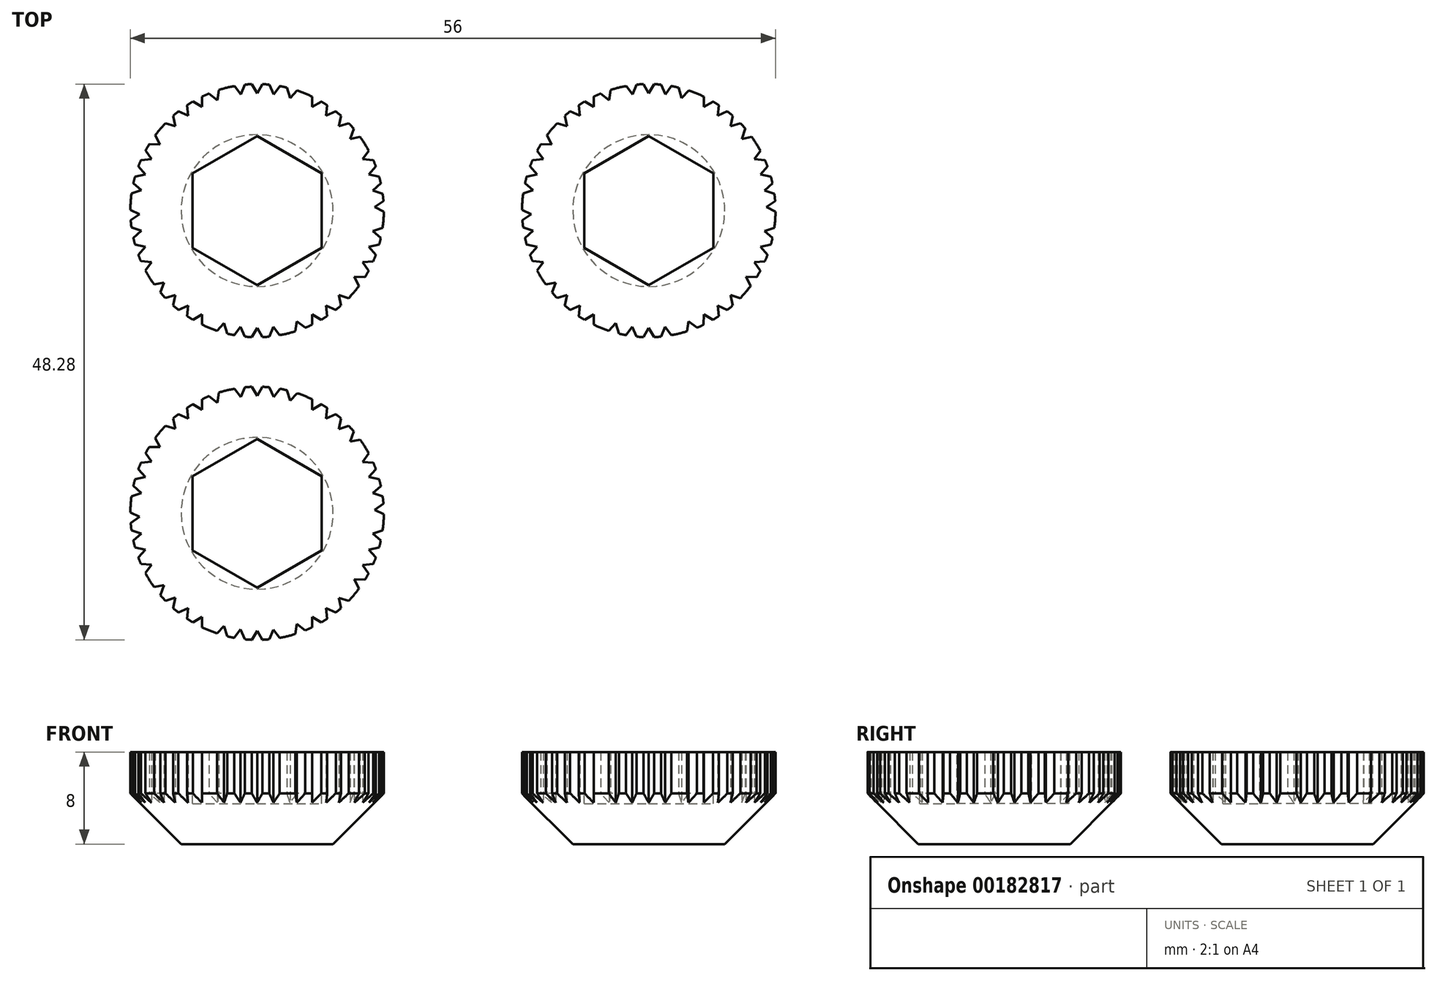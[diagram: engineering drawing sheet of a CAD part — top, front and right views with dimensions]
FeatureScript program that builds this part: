
annotation { "Feature Type Name" : "Feature", "Feature Type Description" : "" }
export const myFeature = defineFeature(function(context is Context, id is Id, definition is map)
    precondition{}
    {
        {
            var Q0;
            Q0=qCreatedBy(makeId("Top.planeOp"),FACE);
            var sketch = newSketch(context, id + "F0", { "sketchPlane" : qUnion([Q0])});
            skCircle(sketch, "E0", {"center": v(0, 0) * mm, "radius": 11 * mm});
            skCircle(sketch, "E1.cCircle", {"center": v(0, 11) * mm, "radius": 0.4 * mm, "construction": true});
            skLineSegment(sketch, "E1.0", {"start": v(-0.7, 11.4) * mm, "end": v(0.7, 11.4) * mm});
            skLineSegment(sketch, "E1.1", {"start": v(0.7, 11.4) * mm, "end": v(0, 10.2) * mm});
            skLineSegment(sketch, "E1.2", {"start": v(0, 10.2) * mm, "end": v(-0.7, 11.4) * mm});
            skPoint(sketch, "E1.0.midPoint", {"position": v(0, 11.4) * mm});
            skLineSegment(sketch, "E2.1.0", {"start": v(-6, 8.25) * mm, "end": v(-7.26, 8.82) * mm});
            skCircle(sketch, "E2.1.1", {"center": v(-6.47, 8.9) * mm, "radius": 0.4 * mm, "construction": true});
            skPoint(sketch, "E2.1.2", {"position": v(-6.7, 9.22) * mm});
            skLineSegment(sketch, "E2.1.3", {"start": v(-7.26, 8.82) * mm, "end": v(-6.14, 9.63) * mm});
            skLineSegment(sketch, "E2.1.4", {"start": v(-6.14, 9.63) * mm, "end": v(-6, 8.25) * mm});
            skLineSegment(sketch, "E2.2.0", {"start": v(-9.7, 3.15) * mm, "end": v(-11.06, 2.86) * mm});
            skCircle(sketch, "E2.2.1", {"center": v(-10.46, 3.4) * mm, "radius": 0.4 * mm, "construction": true});
            skPoint(sketch, "E2.2.2", {"position": v(-10.84, 3.52) * mm});
            skLineSegment(sketch, "E2.2.3", {"start": v(-11.06, 2.86) * mm, "end": v(-10.63, 4.18) * mm});
            skLineSegment(sketch, "E2.2.4", {"start": v(-10.63, 4.18) * mm, "end": v(-9.7, 3.15) * mm});
            skLineSegment(sketch, "E2.3.0", {"start": v(-9.7, -3.15) * mm, "end": v(-10.63, -4.18) * mm});
            skCircle(sketch, "E2.3.1", {"center": v(-10.46, -3.4) * mm, "radius": 0.4 * mm, "construction": true});
            skPoint(sketch, "E2.3.2", {"position": v(-10.84, -3.52) * mm});
            skLineSegment(sketch, "E2.3.3", {"start": v(-10.63, -4.18) * mm, "end": v(-11.06, -2.86) * mm});
            skLineSegment(sketch, "E2.3.4", {"start": v(-11.06, -2.86) * mm, "end": v(-9.7, -3.15) * mm});
            skLineSegment(sketch, "E2.4.0", {"start": v(-6, -8.25) * mm, "end": v(-6.14, -9.63) * mm});
            skCircle(sketch, "E2.4.1", {"center": v(-6.47, -8.9) * mm, "radius": 0.4 * mm, "construction": true});
            skPoint(sketch, "E2.4.2", {"position": v(-6.7, -9.22) * mm});
            skLineSegment(sketch, "E2.4.3", {"start": v(-6.14, -9.63) * mm, "end": v(-7.26, -8.82) * mm});
            skLineSegment(sketch, "E2.4.4", {"start": v(-7.26, -8.82) * mm, "end": v(-6, -8.25) * mm});
            skLineSegment(sketch, "E2.5.0", {"start": v(0, -10.2) * mm, "end": v(0.7, -11.4) * mm});
            skCircle(sketch, "E2.5.1", {"center": v(0, -11) * mm, "radius": 0.4 * mm, "construction": true});
            skPoint(sketch, "E2.5.2", {"position": v(0, -11.4) * mm});
            skLineSegment(sketch, "E2.5.3", {"start": v(0.7, -11.4) * mm, "end": v(-0.7, -11.4) * mm});
            skLineSegment(sketch, "E2.5.4", {"start": v(-0.7, -11.4) * mm, "end": v(0, -10.2) * mm});
            skLineSegment(sketch, "E2.6.0", {"start": v(6, -8.25) * mm, "end": v(7.26, -8.82) * mm});
            skCircle(sketch, "E2.6.1", {"center": v(6.47, -8.9) * mm, "radius": 0.4 * mm, "construction": true});
            skPoint(sketch, "E2.6.2", {"position": v(6.7, -9.22) * mm});
            skLineSegment(sketch, "E2.6.3", {"start": v(7.26, -8.82) * mm, "end": v(6.14, -9.63) * mm});
            skLineSegment(sketch, "E2.6.4", {"start": v(6.14, -9.63) * mm, "end": v(6, -8.25) * mm});
            skLineSegment(sketch, "E2.7.0", {"start": v(9.7, -3.15) * mm, "end": v(11.06, -2.86) * mm});
            skCircle(sketch, "E2.7.1", {"center": v(10.46, -3.4) * mm, "radius": 0.4 * mm, "construction": true});
            skPoint(sketch, "E2.7.2", {"position": v(10.84, -3.52) * mm});
            skLineSegment(sketch, "E2.7.3", {"start": v(11.06, -2.86) * mm, "end": v(10.63, -4.18) * mm});
            skLineSegment(sketch, "E2.7.4", {"start": v(10.63, -4.18) * mm, "end": v(9.7, -3.15) * mm});
            skLineSegment(sketch, "E2.8.0", {"start": v(9.7, 3.15) * mm, "end": v(10.63, 4.18) * mm});
            skCircle(sketch, "E2.8.1", {"center": v(10.46, 3.4) * mm, "radius": 0.4 * mm, "construction": true});
            skPoint(sketch, "E2.8.2", {"position": v(10.84, 3.52) * mm});
            skLineSegment(sketch, "E2.8.3", {"start": v(10.63, 4.18) * mm, "end": v(11.06, 2.86) * mm});
            skLineSegment(sketch, "E2.8.4", {"start": v(11.06, 2.86) * mm, "end": v(9.7, 3.15) * mm});
            skLineSegment(sketch, "E2.9.0", {"start": v(6, 8.25) * mm, "end": v(6.14, 9.63) * mm});
            skCircle(sketch, "E2.9.1", {"center": v(6.47, 8.9) * mm, "radius": 0.4 * mm, "construction": true});
            skPoint(sketch, "E2.9.2", {"position": v(6.7, 9.22) * mm});
            skLineSegment(sketch, "E2.9.3", {"start": v(6.14, 9.63) * mm, "end": v(7.26, 8.82) * mm});
            skLineSegment(sketch, "E2.9.4", {"start": v(7.26, 8.82) * mm, "end": v(6, 8.25) * mm});
            skCircle(sketch, "E3.cCircle", {"center": v(-9.89, 4.82) * mm, "radius": 0.4 * mm, "construction": true});
            skLineSegment(sketch, "E3.0", {"start": v(-9.16, 4.49) * mm, "end": v(-10.54, 4.35) * mm});
            skLineSegment(sketch, "E3.1", {"start": v(-10.54, 4.35) * mm, "end": v(-9.96, 5.61) * mm});
            skLineSegment(sketch, "E3.2", {"start": v(-9.96, 5.61) * mm, "end": v(-9.16, 4.49) * mm});
            skPoint(sketch, "E3.0.midPoint", {"position": v(-9.85, 4.42) * mm});
            skLineSegment(sketch, "E4.1.0", {"start": v(-11.36, -1.31) * mm, "end": v(-10.05, -1.75) * mm});
            skLineSegment(sketch, "E4.1.1", {"start": v(-11.09, -2.67) * mm, "end": v(-11.36, -1.31) * mm});
            skLineSegment(sketch, "E4.1.2", {"start": v(-10.05, -1.75) * mm, "end": v(-11.09, -2.67) * mm});
            skCircle(sketch, "E4.1.3", {"center": v(-10.83, -1.91) * mm, "radius": 0.4 * mm, "construction": true});
            skLineSegment(sketch, "E4.2.0", {"start": v(-8.42, -7.74) * mm, "end": v(-7.1, -7.33) * mm});
            skLineSegment(sketch, "E4.2.1", {"start": v(-7.4, -8.68) * mm, "end": v(-8.42, -7.74) * mm});
            skLineSegment(sketch, "E4.2.2", {"start": v(-7.1, -7.33) * mm, "end": v(-7.4, -8.68) * mm});
            skCircle(sketch, "E4.2.3", {"center": v(-7.64, -7.92) * mm, "radius": 0.4 * mm, "construction": true});
            skLineSegment(sketch, "E4.3.0", {"start": v(-2.26, -11.21) * mm, "end": v(-1.44, -10.1) * mm});
            skLineSegment(sketch, "E4.3.1", {"start": v(-0.88, -11.37) * mm, "end": v(-2.26, -11.21) * mm});
            skLineSegment(sketch, "E4.3.2", {"start": v(-1.44, -10.1) * mm, "end": v(-0.88, -11.37) * mm});
            skCircle(sketch, "E4.3.3", {"center": v(-1.53, -10.9) * mm, "radius": 0.4 * mm, "construction": true});
            skLineSegment(sketch, "E4.4.0", {"start": v(4.76, -10.4) * mm, "end": v(4.77, -9.01) * mm});
            skLineSegment(sketch, "E4.4.1", {"start": v(5.97, -9.72) * mm, "end": v(4.76, -10.4) * mm});
            skLineSegment(sketch, "E4.4.2", {"start": v(4.77, -9.01) * mm, "end": v(5.97, -9.72) * mm});
            skCircle(sketch, "E4.4.3", {"center": v(5.17, -9.71) * mm, "radius": 0.4 * mm, "construction": true});
            skLineSegment(sketch, "E4.5.0", {"start": v(9.96, -5.61) * mm, "end": v(9.16, -4.49) * mm});
            skLineSegment(sketch, "E4.5.1", {"start": v(10.54, -4.35) * mm, "end": v(9.96, -5.61) * mm});
            skLineSegment(sketch, "E4.5.2", {"start": v(9.16, -4.49) * mm, "end": v(10.54, -4.35) * mm});
            skCircle(sketch, "E4.5.3", {"center": v(9.89, -4.82) * mm, "radius": 0.4 * mm, "construction": true});
            skLineSegment(sketch, "E4.6.0", {"start": v(11.36, 1.31) * mm, "end": v(10.05, 1.75) * mm});
            skLineSegment(sketch, "E4.6.1", {"start": v(11.09, 2.67) * mm, "end": v(11.36, 1.31) * mm});
            skLineSegment(sketch, "E4.6.2", {"start": v(10.05, 1.75) * mm, "end": v(11.09, 2.67) * mm});
            skCircle(sketch, "E4.6.3", {"center": v(10.83, 1.91) * mm, "radius": 0.4 * mm, "construction": true});
            skLineSegment(sketch, "E4.7.0", {"start": v(8.42, 7.74) * mm, "end": v(7.1, 7.33) * mm});
            skLineSegment(sketch, "E4.7.1", {"start": v(7.4, 8.68) * mm, "end": v(8.42, 7.74) * mm});
            skLineSegment(sketch, "E4.7.2", {"start": v(7.1, 7.33) * mm, "end": v(7.4, 8.68) * mm});
            skCircle(sketch, "E4.7.3", {"center": v(7.64, 7.92) * mm, "radius": 0.4 * mm, "construction": true});
            skLineSegment(sketch, "E4.8.0", {"start": v(2.26, 11.21) * mm, "end": v(1.44, 10.1) * mm});
            skLineSegment(sketch, "E4.8.1", {"start": v(0.88, 11.37) * mm, "end": v(2.26, 11.21) * mm});
            skLineSegment(sketch, "E4.8.2", {"start": v(1.44, 10.1) * mm, "end": v(0.88, 11.37) * mm});
            skCircle(sketch, "E4.8.3", {"center": v(1.53, 10.9) * mm, "radius": 0.4 * mm, "construction": true});
            skLineSegment(sketch, "E4.9.0", {"start": v(-4.76, 10.4) * mm, "end": v(-4.77, 9.01) * mm});
            skLineSegment(sketch, "E4.9.1", {"start": v(-5.97, 9.72) * mm, "end": v(-4.76, 10.4) * mm});
            skLineSegment(sketch, "E4.9.2", {"start": v(-4.77, 9.01) * mm, "end": v(-5.97, 9.72) * mm});
            skCircle(sketch, "E4.9.3", {"center": v(-5.17, 9.71) * mm, "radius": 0.4 * mm, "construction": true});
            skCircle(sketch, "E5.cCircle", {"center": v(-9.11, 6.16) * mm, "radius": 0.4 * mm, "construction": true});
            skLineSegment(sketch, "E5.0", {"start": v(-9.09, 6.96) * mm, "end": v(-8.43, 5.75) * mm});
            skLineSegment(sketch, "E5.1", {"start": v(-8.43, 5.75) * mm, "end": v(-9.81, 5.78) * mm});
            skLineSegment(sketch, "E5.2", {"start": v(-9.81, 5.78) * mm, "end": v(-9.09, 6.96) * mm});
            skPoint(sketch, "E5.0.midPoint", {"position": v(-8.76, 6.35) * mm});
            skLineSegment(sketch, "E6.1.0", {"start": v(-11.34, -1.09) * mm, "end": v(-11.45, 0.3) * mm});
            skLineSegment(sketch, "E6.1.1", {"start": v(-10.2, -0.3) * mm, "end": v(-11.34, -1.09) * mm});
            skPoint(sketch, "E6.1.2", {"position": v(-10.82, 0) * mm});
            skCircle(sketch, "E6.1.3", {"center": v(-11, -0.37) * mm, "radius": 0.4 * mm, "construction": true});
            skLineSegment(sketch, "E6.1.4", {"start": v(-11.45, 0.3) * mm, "end": v(-10.2, -0.3) * mm});
            skLineSegment(sketch, "E6.2.0", {"start": v(-8.53, -7.55) * mm, "end": v(-9.43, -6.5) * mm});
            skLineSegment(sketch, "E6.2.1", {"start": v(-8.07, -6.24) * mm, "end": v(-8.53, -7.55) * mm});
            skPoint(sketch, "E6.2.2", {"position": v(-8.75, -6.37) * mm});
            skCircle(sketch, "E6.2.3", {"center": v(-8.68, -6.76) * mm, "radius": 0.4 * mm, "construction": true});
            skLineSegment(sketch, "E6.2.4", {"start": v(-9.43, -6.5) * mm, "end": v(-8.07, -6.24) * mm});
            skLineSegment(sketch, "E6.3.0", {"start": v(-2.47, -11.12) * mm, "end": v(-3.82, -10.8) * mm});
            skLineSegment(sketch, "E6.3.1", {"start": v(-2.86, -9.8) * mm, "end": v(-2.47, -11.12) * mm});
            skPoint(sketch, "E6.3.2", {"position": v(-3.34, -10.3) * mm});
            skCircle(sketch, "E6.3.3", {"center": v(-3.05, -10.57) * mm, "radius": 0.4 * mm, "construction": true});
            skLineSegment(sketch, "E6.3.4", {"start": v(-3.82, -10.8) * mm, "end": v(-2.86, -9.8) * mm});
            skLineSegment(sketch, "E6.4.0", {"start": v(4.54, -10.45) * mm, "end": v(3.26, -10.98) * mm});
            skLineSegment(sketch, "E6.4.1", {"start": v(3.44, -9.6) * mm, "end": v(4.54, -10.45) * mm});
            skPoint(sketch, "E6.4.2", {"position": v(3.35, -10.29) * mm});
            skCircle(sketch, "E6.4.3", {"center": v(3.75, -10.34) * mm, "radius": 0.4 * mm, "construction": true});
            skLineSegment(sketch, "E6.4.4", {"start": v(3.26, -10.98) * mm, "end": v(3.44, -9.6) * mm});
            skLineSegment(sketch, "E6.5.0", {"start": v(9.81, -5.78) * mm, "end": v(9.09, -6.96) * mm});
            skLineSegment(sketch, "E6.5.1", {"start": v(8.43, -5.75) * mm, "end": v(9.81, -5.78) * mm});
            skPoint(sketch, "E6.5.2", {"position": v(8.76, -6.35) * mm});
            skCircle(sketch, "E6.5.3", {"center": v(9.11, -6.16) * mm, "radius": 0.4 * mm, "construction": true});
            skLineSegment(sketch, "E6.5.4", {"start": v(9.09, -6.96) * mm, "end": v(8.43, -5.75) * mm});
            skLineSegment(sketch, "E6.6.0", {"start": v(11.34, 1.09) * mm, "end": v(11.45, -0.3) * mm});
            skLineSegment(sketch, "E6.6.1", {"start": v(10.2, 0.3) * mm, "end": v(11.34, 1.09) * mm});
            skPoint(sketch, "E6.6.2", {"position": v(10.82, 0) * mm});
            skCircle(sketch, "E6.6.3", {"center": v(11, 0.37) * mm, "radius": 0.4 * mm, "construction": true});
            skLineSegment(sketch, "E6.6.4", {"start": v(11.45, -0.3) * mm, "end": v(10.2, 0.3) * mm});
            skLineSegment(sketch, "E6.7.0", {"start": v(8.53, 7.55) * mm, "end": v(9.43, 6.5) * mm});
            skLineSegment(sketch, "E6.7.1", {"start": v(8.07, 6.24) * mm, "end": v(8.53, 7.55) * mm});
            skPoint(sketch, "E6.7.2", {"position": v(8.75, 6.37) * mm});
            skCircle(sketch, "E6.7.3", {"center": v(8.68, 6.76) * mm, "radius": 0.4 * mm, "construction": true});
            skLineSegment(sketch, "E6.7.4", {"start": v(9.43, 6.5) * mm, "end": v(8.07, 6.24) * mm});
            skLineSegment(sketch, "E6.8.0", {"start": v(2.47, 11.12) * mm, "end": v(3.82, 10.8) * mm});
            skLineSegment(sketch, "E6.8.1", {"start": v(2.86, 9.8) * mm, "end": v(2.47, 11.12) * mm});
            skPoint(sketch, "E6.8.2", {"position": v(3.34, 10.3) * mm});
            skCircle(sketch, "E6.8.3", {"center": v(3.05, 10.57) * mm, "radius": 0.4 * mm, "construction": true});
            skLineSegment(sketch, "E6.8.4", {"start": v(3.82, 10.8) * mm, "end": v(2.86, 9.8) * mm});
            skLineSegment(sketch, "E6.9.0", {"start": v(-4.54, 10.45) * mm, "end": v(-3.26, 10.98) * mm});
            skLineSegment(sketch, "E6.9.1", {"start": v(-3.44, 9.6) * mm, "end": v(-4.54, 10.45) * mm});
            skPoint(sketch, "E6.9.2", {"position": v(-3.35, 10.29) * mm});
            skCircle(sketch, "E6.9.3", {"center": v(-3.75, 10.34) * mm, "radius": 0.4 * mm, "construction": true});
            skLineSegment(sketch, "E6.9.4", {"start": v(-3.26, 10.98) * mm, "end": v(-3.44, 9.6) * mm});
            skCircle(sketch, "E7.cCircle", {"center": v(-5.18, -9.7) * mm, "radius": 0.4 * mm, "construction": true});
            skLineSegment(sketch, "E7.0", {"start": v(-5.98, -9.71) * mm, "end": v(-4.79, -9) * mm});
            skLineSegment(sketch, "E7.1", {"start": v(-4.79, -9) * mm, "end": v(-4.77, -10.4) * mm});
            skLineSegment(sketch, "E7.2", {"start": v(-4.77, -10.4) * mm, "end": v(-5.98, -9.71) * mm});
            skPoint(sketch, "E7.0.midPoint", {"position": v(-5.38, -9.36) * mm});
            skLineSegment(sketch, "E8.1.0", {"start": v(1.42, -10.1) * mm, "end": v(2.25, -11.21) * mm});
            skLineSegment(sketch, "E8.1.1", {"start": v(2.25, -11.21) * mm, "end": v(0.87, -11.37) * mm});
            skLineSegment(sketch, "E8.1.2", {"start": v(0.87, -11.37) * mm, "end": v(1.42, -10.1) * mm});
            skCircle(sketch, "E8.1.3", {"center": v(1.51, -10.9) * mm, "radius": 0.4 * mm, "construction": true});
            skLineSegment(sketch, "E8.2.0", {"start": v(7.09, -7.34) * mm, "end": v(8.4, -7.75) * mm});
            skLineSegment(sketch, "E8.2.1", {"start": v(8.4, -7.75) * mm, "end": v(7.4, -8.69) * mm});
            skLineSegment(sketch, "E8.2.2", {"start": v(7.4, -8.69) * mm, "end": v(7.09, -7.34) * mm});
            skCircle(sketch, "E8.2.3", {"center": v(7.63, -7.92) * mm, "radius": 0.4 * mm, "construction": true});
            skLineSegment(sketch, "E8.3.0", {"start": v(10.05, -1.77) * mm, "end": v(11.36, -1.33) * mm});
            skLineSegment(sketch, "E8.3.1", {"start": v(11.36, -1.33) * mm, "end": v(11.09, -2.68) * mm});
            skLineSegment(sketch, "E8.3.2", {"start": v(11.09, -2.68) * mm, "end": v(10.05, -1.77) * mm});
            skCircle(sketch, "E8.3.3", {"center": v(10.83, -1.93) * mm, "radius": 0.4 * mm, "construction": true});
            skLineSegment(sketch, "E8.4.0", {"start": v(9.17, 4.47) * mm, "end": v(9.97, 5.6) * mm});
            skLineSegment(sketch, "E8.4.1", {"start": v(9.97, 5.6) * mm, "end": v(10.55, 4.34) * mm});
            skLineSegment(sketch, "E8.4.2", {"start": v(10.55, 4.34) * mm, "end": v(9.17, 4.47) * mm});
            skCircle(sketch, "E8.4.3", {"center": v(9.9, 4.8) * mm, "radius": 0.4 * mm, "construction": true});
            skLineSegment(sketch, "E8.5.0", {"start": v(4.79, 9) * mm, "end": v(4.77, 10.4) * mm});
            skLineSegment(sketch, "E8.5.1", {"start": v(4.77, 10.4) * mm, "end": v(5.98, 9.71) * mm});
            skLineSegment(sketch, "E8.5.2", {"start": v(5.98, 9.71) * mm, "end": v(4.79, 9) * mm});
            skCircle(sketch, "E8.5.3", {"center": v(5.18, 9.7) * mm, "radius": 0.4 * mm, "construction": true});
            skLineSegment(sketch, "E8.6.0", {"start": v(-1.42, 10.1) * mm, "end": v(-2.25, 11.21) * mm});
            skLineSegment(sketch, "E8.6.1", {"start": v(-2.25, 11.21) * mm, "end": v(-0.87, 11.37) * mm});
            skLineSegment(sketch, "E8.6.2", {"start": v(-0.87, 11.37) * mm, "end": v(-1.42, 10.1) * mm});
            skCircle(sketch, "E8.6.3", {"center": v(-1.51, 10.9) * mm, "radius": 0.4 * mm, "construction": true});
            skLineSegment(sketch, "E8.7.0", {"start": v(-7.09, 7.34) * mm, "end": v(-8.4, 7.75) * mm});
            skLineSegment(sketch, "E8.7.1", {"start": v(-8.4, 7.75) * mm, "end": v(-7.4, 8.69) * mm});
            skLineSegment(sketch, "E8.7.2", {"start": v(-7.4, 8.69) * mm, "end": v(-7.09, 7.34) * mm});
            skCircle(sketch, "E8.7.3", {"center": v(-7.63, 7.92) * mm, "radius": 0.4 * mm, "construction": true});
            skLineSegment(sketch, "E8.8.0", {"start": v(-10.05, 1.77) * mm, "end": v(-11.36, 1.33) * mm});
            skLineSegment(sketch, "E8.8.1", {"start": v(-11.36, 1.33) * mm, "end": v(-11.09, 2.68) * mm});
            skLineSegment(sketch, "E8.8.2", {"start": v(-11.09, 2.68) * mm, "end": v(-10.05, 1.77) * mm});
            skCircle(sketch, "E8.8.3", {"center": v(-10.83, 1.93) * mm, "radius": 0.4 * mm, "construction": true});
            skLineSegment(sketch, "E8.9.0", {"start": v(-9.17, -4.47) * mm, "end": v(-9.97, -5.6) * mm});
            skLineSegment(sketch, "E8.9.1", {"start": v(-9.97, -5.6) * mm, "end": v(-10.55, -4.34) * mm});
            skLineSegment(sketch, "E8.9.2", {"start": v(-10.55, -4.34) * mm, "end": v(-9.17, -4.47) * mm});
            skCircle(sketch, "E8.9.3", {"center": v(-9.9, -4.8) * mm, "radius": 0.4 * mm, "construction": true});
            skSolve(sketch);
        }
        {
            var Q0;
            Q0=makeQuery(id+"F0.imprint","IMPRINT",FACE,{"disambiguationData":[TD([[makeQuery(id+"F0.imprint","IMPRINT",EDGE,{"derivedFrom":sQuery(id+"F0.wireOp",EDGE,"E0")}),1.0]])]});
            var Q1;
            Q1=sQuery(id+"F0.wireOp",EDGE,"E0");
            extrude(context, id + "F1", {"entities" : qUnion([Q0]), "surfaceEntities" : qUnion([Q1]), "depth" : 8 * mm});
        }
        {
            var Q0;
            Q0=makeQuery(id+"F1.opExtrude","CAP_FACE",FACE,{"disambiguationData":[OSD([sQuery(id+"F0.wireOp",EDGE,"E0")])],"isStart":false});
            var sketch = newSketch(context, id + "F2", { "sketchPlane" : qUnion([Q0])});
            skCircle(sketch, "E9.cCircle", {"center": v(0, 0) * mm, "radius": 5.6 * mm, "construction": true});
            skLineSegment(sketch, "E9.0", {"start": v(5.6, 3.23) * mm, "end": v(5.6, -3.23) * mm});
            skLineSegment(sketch, "E9.1", {"start": v(5.6, -3.23) * mm, "end": v(0, -6.47) * mm});
            skLineSegment(sketch, "E9.2", {"start": v(0, -6.47) * mm, "end": v(-5.6, -3.23) * mm});
            skLineSegment(sketch, "E9.3", {"start": v(-5.6, -3.23) * mm, "end": v(-5.6, 3.23) * mm});
            skLineSegment(sketch, "E9.4", {"start": v(-5.6, 3.23) * mm, "end": v(0, 6.47) * mm});
            skLineSegment(sketch, "E9.5", {"start": v(0, 6.47) * mm, "end": v(5.6, 3.23) * mm});
            skPoint(sketch, "E9.0.midPoint", {"position": v(5.6, 0) * mm});
            skSolve(sketch);
        }
        {
            var Q0;
            Q0=makeQuery(id+"F2.imprint","IMPRINT",FACE,{"disambiguationData":[TD([[makeQuery(id+"F2.imprint","IMPRINT",EDGE,{"derivedFrom":sQuery(id+"F2.wireOp",EDGE,"E9.0")}),-1.0]])]});
            extrude(context, id + "F3", {"entities" : qUnion([Q0]), "operationType" : NewBodyOperationType.REMOVE, "oppositeDirection" : true, "depth" : 4.5 * mm});
        }
        {
            var Q0;
            Q0=qCreatedBy(makeId("Front.planeOp"),FACE);
            var sketch = newSketch(context, id + "F4", { "sketchPlane" : qUnion([Q0])});
            skLineSegment(sketch, "E10", {"start": v(11.1, 4.5) * mm, "end": v(11.1, 0) * mm});
            skLineSegment(sketch, "E11", {"start": v(11.1, 0) * mm, "end": v(6.6, 0) * mm});
            skLineSegment(sketch, "E12", {"start": v(11.1, 4.5) * mm, "end": v(6.6, 0) * mm});
            skSolve(sketch);
        }
        {
            var Q0;
            Q0=qCreatedBy(makeId("Front.planeOp"),FACE);
            var sketch = newSketch(context, id + "F5", { "sketchPlane" : qUnion([Q0])});
            skLineSegment(sketch, "E13", {"start": v(0, 0) * mm, "end": v(0, -10.93) * mm});
            skSolve(sketch);
        }
        {
            var Q0;
            Q0 = qSketchRegion(id + "F4", true);
            var Q1;
            Q1=sQuery(id+"F5.wireOp",EDGE,"E13");
            revolve(context, id + "F6", {"operationType" : NewBodyOperationType.REMOVE, "entities" : qUnion([Q0]), "axis" : qUnion([Q1]), "revolveType" : RevolveType.FULL, "oppositeDirection" : true});
        }
        {
            var Q0;
            Q0=makeQuery(id+"F1.opExtrude","SWEPT_BODY",BODY,{"disambiguationData":[OSD([sQuery(id+"F0.wireOp",EDGE,"E0"),sQuery(id+"F0.wireOp",EDGE,"E1.1"),sQuery(id+"F0.wireOp",EDGE,"E1.2"),sQuery(id+"F0.wireOp",EDGE,"E2.1.0"),sQuery(id+"F0.wireOp",EDGE,"E2.1.4"),sQuery(id+"F0.wireOp",EDGE,"E2.2.0"),sQuery(id+"F0.wireOp",EDGE,"E2.2.4"),sQuery(id+"F0.wireOp",EDGE,"E2.3.0"),sQuery(id+"F0.wireOp",EDGE,"E2.3.4"),sQuery(id+"F0.wireOp",EDGE,"E2.4.0"),sQuery(id+"F0.wireOp",EDGE,"E2.4.4"),sQuery(id+"F0.wireOp",EDGE,"E2.5.0"),sQuery(id+"F0.wireOp",EDGE,"E2.5.4"),sQuery(id+"F0.wireOp",EDGE,"E2.6.0"),sQuery(id+"F0.wireOp",EDGE,"E2.6.4"),sQuery(id+"F0.wireOp",EDGE,"E2.7.0"),sQuery(id+"F0.wireOp",EDGE,"E2.7.4"),sQuery(id+"F0.wireOp",EDGE,"E2.8.0"),sQuery(id+"F0.wireOp",EDGE,"E2.8.4"),sQuery(id+"F0.wireOp",EDGE,"E2.9.0"),sQuery(id+"F0.wireOp",EDGE,"E2.9.4"),sQuery(id+"F0.wireOp",EDGE,"E3.0"),sQuery(id+"F0.wireOp",EDGE,"E3.2"),sQuery(id+"F0.wireOp",EDGE,"E4.1.0"),sQuery(id+"F0.wireOp",EDGE,"E4.1.2"),sQuery(id+"F0.wireOp",EDGE,"E4.2.0"),sQuery(id+"F0.wireOp",EDGE,"E4.2.2"),sQuery(id+"F0.wireOp",EDGE,"E4.3.0"),sQuery(id+"F0.wireOp",EDGE,"E4.3.2"),sQuery(id+"F0.wireOp",EDGE,"E4.4.0"),sQuery(id+"F0.wireOp",EDGE,"E4.4.2"),sQuery(id+"F0.wireOp",EDGE,"E4.5.0"),sQuery(id+"F0.wireOp",EDGE,"E4.5.2"),sQuery(id+"F0.wireOp",EDGE,"E4.6.0"),sQuery(id+"F0.wireOp",EDGE,"E4.6.2"),sQuery(id+"F0.wireOp",EDGE,"E4.7.0"),sQuery(id+"F0.wireOp",EDGE,"E4.7.2"),sQuery(id+"F0.wireOp",EDGE,"E4.8.0"),sQuery(id+"F0.wireOp",EDGE,"E4.8.2"),sQuery(id+"F0.wireOp",EDGE,"E4.9.0"),sQuery(id+"F0.wireOp",EDGE,"E4.9.2"),sQuery(id+"F0.wireOp",EDGE,"E5.0"),sQuery(id+"F0.wireOp",EDGE,"E5.1"),sQuery(id+"F0.wireOp",EDGE,"E6.1.1"),sQuery(id+"F0.wireOp",EDGE,"E6.1.4"),sQuery(id+"F0.wireOp",EDGE,"E6.2.1"),sQuery(id+"F0.wireOp",EDGE,"E6.2.4"),sQuery(id+"F0.wireOp",EDGE,"E6.3.1"),sQuery(id+"F0.wireOp",EDGE,"E6.3.4"),sQuery(id+"F0.wireOp",EDGE,"E6.4.1"),sQuery(id+"F0.wireOp",EDGE,"E6.4.4"),sQuery(id+"F0.wireOp",EDGE,"E6.5.1"),sQuery(id+"F0.wireOp",EDGE,"E6.5.4"),sQuery(id+"F0.wireOp",EDGE,"E6.6.1"),sQuery(id+"F0.wireOp",EDGE,"E6.6.4"),sQuery(id+"F0.wireOp",EDGE,"E6.7.1"),sQuery(id+"F0.wireOp",EDGE,"E6.7.4"),sQuery(id+"F0.wireOp",EDGE,"E6.8.1"),sQuery(id+"F0.wireOp",EDGE,"E6.8.4"),sQuery(id+"F0.wireOp",EDGE,"E6.9.1"),sQuery(id+"F0.wireOp",EDGE,"E6.9.4"),sQuery(id+"F0.wireOp",EDGE,"E7.0"),sQuery(id+"F0.wireOp",EDGE,"E7.1"),sQuery(id+"F0.wireOp",EDGE,"E8.1.0"),sQuery(id+"F0.wireOp",EDGE,"E8.1.2"),sQuery(id+"F0.wireOp",EDGE,"E8.2.0"),sQuery(id+"F0.wireOp",EDGE,"E8.2.2"),sQuery(id+"F0.wireOp",EDGE,"E8.3.0"),sQuery(id+"F0.wireOp",EDGE,"E8.3.2"),sQuery(id+"F0.wireOp",EDGE,"E8.4.0"),sQuery(id+"F0.wireOp",EDGE,"E8.4.2"),sQuery(id+"F0.wireOp",EDGE,"E8.5.0"),sQuery(id+"F0.wireOp",EDGE,"E8.5.2"),sQuery(id+"F0.wireOp",EDGE,"E8.6.0"),sQuery(id+"F0.wireOp",EDGE,"E8.6.2"),sQuery(id+"F0.wireOp",EDGE,"E8.7.0"),sQuery(id+"F0.wireOp",EDGE,"E8.7.2"),sQuery(id+"F0.wireOp",EDGE,"E8.8.0"),sQuery(id+"F0.wireOp",EDGE,"E8.8.2"),sQuery(id+"F0.wireOp",EDGE,"E8.9.0"),sQuery(id+"F0.wireOp",EDGE,"E8.9.2")])]});
            transform(context, id + "F7", {"entities" : qUnion([Q0]), "transformType" : TransformType.TRANSLATION_3D, "dx" : 34 * mm, "dy" : 0 * mm, "dz" : 0 * mm, "makeCopy" : true});
        }
        {
            var Q0;
            Q0=makeQuery(id+"F1.opExtrude","SWEPT_BODY",BODY,{"disambiguationData":[OSD([sQuery(id+"F0.wireOp",EDGE,"E0"),sQuery(id+"F0.wireOp",EDGE,"E1.1"),sQuery(id+"F0.wireOp",EDGE,"E1.2"),sQuery(id+"F0.wireOp",EDGE,"E2.1.0"),sQuery(id+"F0.wireOp",EDGE,"E2.1.4"),sQuery(id+"F0.wireOp",EDGE,"E2.2.0"),sQuery(id+"F0.wireOp",EDGE,"E2.2.4"),sQuery(id+"F0.wireOp",EDGE,"E2.3.0"),sQuery(id+"F0.wireOp",EDGE,"E2.3.4"),sQuery(id+"F0.wireOp",EDGE,"E2.4.0"),sQuery(id+"F0.wireOp",EDGE,"E2.4.4"),sQuery(id+"F0.wireOp",EDGE,"E2.5.0"),sQuery(id+"F0.wireOp",EDGE,"E2.5.4"),sQuery(id+"F0.wireOp",EDGE,"E2.6.0"),sQuery(id+"F0.wireOp",EDGE,"E2.6.4"),sQuery(id+"F0.wireOp",EDGE,"E2.7.0"),sQuery(id+"F0.wireOp",EDGE,"E2.7.4"),sQuery(id+"F0.wireOp",EDGE,"E2.8.0"),sQuery(id+"F0.wireOp",EDGE,"E2.8.4"),sQuery(id+"F0.wireOp",EDGE,"E2.9.0"),sQuery(id+"F0.wireOp",EDGE,"E2.9.4"),sQuery(id+"F0.wireOp",EDGE,"E3.0"),sQuery(id+"F0.wireOp",EDGE,"E3.2"),sQuery(id+"F0.wireOp",EDGE,"E4.1.0"),sQuery(id+"F0.wireOp",EDGE,"E4.1.2"),sQuery(id+"F0.wireOp",EDGE,"E4.2.0"),sQuery(id+"F0.wireOp",EDGE,"E4.2.2"),sQuery(id+"F0.wireOp",EDGE,"E4.3.0"),sQuery(id+"F0.wireOp",EDGE,"E4.3.2"),sQuery(id+"F0.wireOp",EDGE,"E4.4.0"),sQuery(id+"F0.wireOp",EDGE,"E4.4.2"),sQuery(id+"F0.wireOp",EDGE,"E4.5.0"),sQuery(id+"F0.wireOp",EDGE,"E4.5.2"),sQuery(id+"F0.wireOp",EDGE,"E4.6.0"),sQuery(id+"F0.wireOp",EDGE,"E4.6.2"),sQuery(id+"F0.wireOp",EDGE,"E4.7.0"),sQuery(id+"F0.wireOp",EDGE,"E4.7.2"),sQuery(id+"F0.wireOp",EDGE,"E4.8.0"),sQuery(id+"F0.wireOp",EDGE,"E4.8.2"),sQuery(id+"F0.wireOp",EDGE,"E4.9.0"),sQuery(id+"F0.wireOp",EDGE,"E4.9.2"),sQuery(id+"F0.wireOp",EDGE,"E5.0"),sQuery(id+"F0.wireOp",EDGE,"E5.1"),sQuery(id+"F0.wireOp",EDGE,"E6.1.1"),sQuery(id+"F0.wireOp",EDGE,"E6.1.4"),sQuery(id+"F0.wireOp",EDGE,"E6.2.1"),sQuery(id+"F0.wireOp",EDGE,"E6.2.4"),sQuery(id+"F0.wireOp",EDGE,"E6.3.1"),sQuery(id+"F0.wireOp",EDGE,"E6.3.4"),sQuery(id+"F0.wireOp",EDGE,"E6.4.1"),sQuery(id+"F0.wireOp",EDGE,"E6.4.4"),sQuery(id+"F0.wireOp",EDGE,"E6.5.1"),sQuery(id+"F0.wireOp",EDGE,"E6.5.4"),sQuery(id+"F0.wireOp",EDGE,"E6.6.1"),sQuery(id+"F0.wireOp",EDGE,"E6.6.4"),sQuery(id+"F0.wireOp",EDGE,"E6.7.1"),sQuery(id+"F0.wireOp",EDGE,"E6.7.4"),sQuery(id+"F0.wireOp",EDGE,"E6.8.1"),sQuery(id+"F0.wireOp",EDGE,"E6.8.4"),sQuery(id+"F0.wireOp",EDGE,"E6.9.1"),sQuery(id+"F0.wireOp",EDGE,"E6.9.4"),sQuery(id+"F0.wireOp",EDGE,"E7.0"),sQuery(id+"F0.wireOp",EDGE,"E7.1"),sQuery(id+"F0.wireOp",EDGE,"E8.1.0"),sQuery(id+"F0.wireOp",EDGE,"E8.1.2"),sQuery(id+"F0.wireOp",EDGE,"E8.2.0"),sQuery(id+"F0.wireOp",EDGE,"E8.2.2"),sQuery(id+"F0.wireOp",EDGE,"E8.3.0"),sQuery(id+"F0.wireOp",EDGE,"E8.3.2"),sQuery(id+"F0.wireOp",EDGE,"E8.4.0"),sQuery(id+"F0.wireOp",EDGE,"E8.4.2"),sQuery(id+"F0.wireOp",EDGE,"E8.5.0"),sQuery(id+"F0.wireOp",EDGE,"E8.5.2"),sQuery(id+"F0.wireOp",EDGE,"E8.6.0"),sQuery(id+"F0.wireOp",EDGE,"E8.6.2"),sQuery(id+"F0.wireOp",EDGE,"E8.7.0"),sQuery(id+"F0.wireOp",EDGE,"E8.7.2"),sQuery(id+"F0.wireOp",EDGE,"E8.8.0"),sQuery(id+"F0.wireOp",EDGE,"E8.8.2"),sQuery(id+"F0.wireOp",EDGE,"E8.9.0"),sQuery(id+"F0.wireOp",EDGE,"E8.9.2")])]});
            transform(context, id + "F8", {"entities" : qUnion([Q0]), "transformType" : TransformType.TRANSLATION_3D, "dx" : -24 * mm, "dy" : 9 * mm, "dz" : -34 * mm, "makeCopy" : true});
        }
        {
            var Q0;
            Q0=makeQuery(id+"F8.opPattern","COPY",BODY,{"derivedFrom":makeQuery(id+"F1.opExtrude","SWEPT_BODY",BODY,{"disambiguationData":[OSD([sQuery(id+"F0.wireOp",EDGE,"E0"),sQuery(id+"F0.wireOp",EDGE,"E1.1"),sQuery(id+"F0.wireOp",EDGE,"E1.2"),sQuery(id+"F0.wireOp",EDGE,"E2.1.0"),sQuery(id+"F0.wireOp",EDGE,"E2.1.4"),sQuery(id+"F0.wireOp",EDGE,"E2.2.0"),sQuery(id+"F0.wireOp",EDGE,"E2.2.4"),sQuery(id+"F0.wireOp",EDGE,"E2.3.0"),sQuery(id+"F0.wireOp",EDGE,"E2.3.4"),sQuery(id+"F0.wireOp",EDGE,"E2.4.0"),sQuery(id+"F0.wireOp",EDGE,"E2.4.4"),sQuery(id+"F0.wireOp",EDGE,"E2.5.0"),sQuery(id+"F0.wireOp",EDGE,"E2.5.4"),sQuery(id+"F0.wireOp",EDGE,"E2.6.0"),sQuery(id+"F0.wireOp",EDGE,"E2.6.4"),sQuery(id+"F0.wireOp",EDGE,"E2.7.0"),sQuery(id+"F0.wireOp",EDGE,"E2.7.4"),sQuery(id+"F0.wireOp",EDGE,"E2.8.0"),sQuery(id+"F0.wireOp",EDGE,"E2.8.4"),sQuery(id+"F0.wireOp",EDGE,"E2.9.0"),sQuery(id+"F0.wireOp",EDGE,"E2.9.4"),sQuery(id+"F0.wireOp",EDGE,"E3.0"),sQuery(id+"F0.wireOp",EDGE,"E3.2"),sQuery(id+"F0.wireOp",EDGE,"E4.1.0"),sQuery(id+"F0.wireOp",EDGE,"E4.1.2"),sQuery(id+"F0.wireOp",EDGE,"E4.2.0"),sQuery(id+"F0.wireOp",EDGE,"E4.2.2"),sQuery(id+"F0.wireOp",EDGE,"E4.3.0"),sQuery(id+"F0.wireOp",EDGE,"E4.3.2"),sQuery(id+"F0.wireOp",EDGE,"E4.4.0"),sQuery(id+"F0.wireOp",EDGE,"E4.4.2"),sQuery(id+"F0.wireOp",EDGE,"E4.5.0"),sQuery(id+"F0.wireOp",EDGE,"E4.5.2"),sQuery(id+"F0.wireOp",EDGE,"E4.6.0"),sQuery(id+"F0.wireOp",EDGE,"E4.6.2"),sQuery(id+"F0.wireOp",EDGE,"E4.7.0"),sQuery(id+"F0.wireOp",EDGE,"E4.7.2"),sQuery(id+"F0.wireOp",EDGE,"E4.8.0"),sQuery(id+"F0.wireOp",EDGE,"E4.8.2"),sQuery(id+"F0.wireOp",EDGE,"E4.9.0"),sQuery(id+"F0.wireOp",EDGE,"E4.9.2"),sQuery(id+"F0.wireOp",EDGE,"E5.0"),sQuery(id+"F0.wireOp",EDGE,"E5.1"),sQuery(id+"F0.wireOp",EDGE,"E6.1.1"),sQuery(id+"F0.wireOp",EDGE,"E6.1.4"),sQuery(id+"F0.wireOp",EDGE,"E6.2.1"),sQuery(id+"F0.wireOp",EDGE,"E6.2.4"),sQuery(id+"F0.wireOp",EDGE,"E6.3.1"),sQuery(id+"F0.wireOp",EDGE,"E6.3.4"),sQuery(id+"F0.wireOp",EDGE,"E6.4.1"),sQuery(id+"F0.wireOp",EDGE,"E6.4.4"),sQuery(id+"F0.wireOp",EDGE,"E6.5.1"),sQuery(id+"F0.wireOp",EDGE,"E6.5.4"),sQuery(id+"F0.wireOp",EDGE,"E6.6.1"),sQuery(id+"F0.wireOp",EDGE,"E6.6.4"),sQuery(id+"F0.wireOp",EDGE,"E6.7.1"),sQuery(id+"F0.wireOp",EDGE,"E6.7.4"),sQuery(id+"F0.wireOp",EDGE,"E6.8.1"),sQuery(id+"F0.wireOp",EDGE,"E6.8.4"),sQuery(id+"F0.wireOp",EDGE,"E6.9.1"),sQuery(id+"F0.wireOp",EDGE,"E6.9.4"),sQuery(id+"F0.wireOp",EDGE,"E7.0"),sQuery(id+"F0.wireOp",EDGE,"E7.1"),sQuery(id+"F0.wireOp",EDGE,"E8.1.0"),sQuery(id+"F0.wireOp",EDGE,"E8.1.2"),sQuery(id+"F0.wireOp",EDGE,"E8.2.0"),sQuery(id+"F0.wireOp",EDGE,"E8.2.2"),sQuery(id+"F0.wireOp",EDGE,"E8.3.0"),sQuery(id+"F0.wireOp",EDGE,"E8.3.2"),sQuery(id+"F0.wireOp",EDGE,"E8.4.0"),sQuery(id+"F0.wireOp",EDGE,"E8.4.2"),sQuery(id+"F0.wireOp",EDGE,"E8.5.0"),sQuery(id+"F0.wireOp",EDGE,"E8.5.2"),sQuery(id+"F0.wireOp",EDGE,"E8.6.0"),sQuery(id+"F0.wireOp",EDGE,"E8.6.2"),sQuery(id+"F0.wireOp",EDGE,"E8.7.0"),sQuery(id+"F0.wireOp",EDGE,"E8.7.2"),sQuery(id+"F0.wireOp",EDGE,"E8.8.0"),sQuery(id+"F0.wireOp",EDGE,"E8.8.2"),sQuery(id+"F0.wireOp",EDGE,"E8.9.0"),sQuery(id+"F0.wireOp",EDGE,"E8.9.2")])]}),"instanceName":"1"});
            deleteBodies(context, id + "F9", {"entities" : qUnion([Q0])});
        }
        {
            var Q0;
            Q0=makeQuery(id+"F1.opExtrude","SWEPT_BODY",BODY,{"disambiguationData":[OSD([sQuery(id+"F0.wireOp",EDGE,"E0"),sQuery(id+"F0.wireOp",EDGE,"E1.1"),sQuery(id+"F0.wireOp",EDGE,"E1.2"),sQuery(id+"F0.wireOp",EDGE,"E2.1.0"),sQuery(id+"F0.wireOp",EDGE,"E2.1.4"),sQuery(id+"F0.wireOp",EDGE,"E2.2.0"),sQuery(id+"F0.wireOp",EDGE,"E2.2.4"),sQuery(id+"F0.wireOp",EDGE,"E2.3.0"),sQuery(id+"F0.wireOp",EDGE,"E2.3.4"),sQuery(id+"F0.wireOp",EDGE,"E2.4.0"),sQuery(id+"F0.wireOp",EDGE,"E2.4.4"),sQuery(id+"F0.wireOp",EDGE,"E2.5.0"),sQuery(id+"F0.wireOp",EDGE,"E2.5.4"),sQuery(id+"F0.wireOp",EDGE,"E2.6.0"),sQuery(id+"F0.wireOp",EDGE,"E2.6.4"),sQuery(id+"F0.wireOp",EDGE,"E2.7.0"),sQuery(id+"F0.wireOp",EDGE,"E2.7.4"),sQuery(id+"F0.wireOp",EDGE,"E2.8.0"),sQuery(id+"F0.wireOp",EDGE,"E2.8.4"),sQuery(id+"F0.wireOp",EDGE,"E2.9.0"),sQuery(id+"F0.wireOp",EDGE,"E2.9.4"),sQuery(id+"F0.wireOp",EDGE,"E3.0"),sQuery(id+"F0.wireOp",EDGE,"E3.2"),sQuery(id+"F0.wireOp",EDGE,"E4.1.0"),sQuery(id+"F0.wireOp",EDGE,"E4.1.2"),sQuery(id+"F0.wireOp",EDGE,"E4.2.0"),sQuery(id+"F0.wireOp",EDGE,"E4.2.2"),sQuery(id+"F0.wireOp",EDGE,"E4.3.0"),sQuery(id+"F0.wireOp",EDGE,"E4.3.2"),sQuery(id+"F0.wireOp",EDGE,"E4.4.0"),sQuery(id+"F0.wireOp",EDGE,"E4.4.2"),sQuery(id+"F0.wireOp",EDGE,"E4.5.0"),sQuery(id+"F0.wireOp",EDGE,"E4.5.2"),sQuery(id+"F0.wireOp",EDGE,"E4.6.0"),sQuery(id+"F0.wireOp",EDGE,"E4.6.2"),sQuery(id+"F0.wireOp",EDGE,"E4.7.0"),sQuery(id+"F0.wireOp",EDGE,"E4.7.2"),sQuery(id+"F0.wireOp",EDGE,"E4.8.0"),sQuery(id+"F0.wireOp",EDGE,"E4.8.2"),sQuery(id+"F0.wireOp",EDGE,"E4.9.0"),sQuery(id+"F0.wireOp",EDGE,"E4.9.2"),sQuery(id+"F0.wireOp",EDGE,"E5.0"),sQuery(id+"F0.wireOp",EDGE,"E5.1"),sQuery(id+"F0.wireOp",EDGE,"E6.1.1"),sQuery(id+"F0.wireOp",EDGE,"E6.1.4"),sQuery(id+"F0.wireOp",EDGE,"E6.2.1"),sQuery(id+"F0.wireOp",EDGE,"E6.2.4"),sQuery(id+"F0.wireOp",EDGE,"E6.3.1"),sQuery(id+"F0.wireOp",EDGE,"E6.3.4"),sQuery(id+"F0.wireOp",EDGE,"E6.4.1"),sQuery(id+"F0.wireOp",EDGE,"E6.4.4"),sQuery(id+"F0.wireOp",EDGE,"E6.5.1"),sQuery(id+"F0.wireOp",EDGE,"E6.5.4"),sQuery(id+"F0.wireOp",EDGE,"E6.6.1"),sQuery(id+"F0.wireOp",EDGE,"E6.6.4"),sQuery(id+"F0.wireOp",EDGE,"E6.7.1"),sQuery(id+"F0.wireOp",EDGE,"E6.7.4"),sQuery(id+"F0.wireOp",EDGE,"E6.8.1"),sQuery(id+"F0.wireOp",EDGE,"E6.8.4"),sQuery(id+"F0.wireOp",EDGE,"E6.9.1"),sQuery(id+"F0.wireOp",EDGE,"E6.9.4"),sQuery(id+"F0.wireOp",EDGE,"E7.0"),sQuery(id+"F0.wireOp",EDGE,"E7.1"),sQuery(id+"F0.wireOp",EDGE,"E8.1.0"),sQuery(id+"F0.wireOp",EDGE,"E8.1.2"),sQuery(id+"F0.wireOp",EDGE,"E8.2.0"),sQuery(id+"F0.wireOp",EDGE,"E8.2.2"),sQuery(id+"F0.wireOp",EDGE,"E8.3.0"),sQuery(id+"F0.wireOp",EDGE,"E8.3.2"),sQuery(id+"F0.wireOp",EDGE,"E8.4.0"),sQuery(id+"F0.wireOp",EDGE,"E8.4.2"),sQuery(id+"F0.wireOp",EDGE,"E8.5.0"),sQuery(id+"F0.wireOp",EDGE,"E8.5.2"),sQuery(id+"F0.wireOp",EDGE,"E8.6.0"),sQuery(id+"F0.wireOp",EDGE,"E8.6.2"),sQuery(id+"F0.wireOp",EDGE,"E8.7.0"),sQuery(id+"F0.wireOp",EDGE,"E8.7.2"),sQuery(id+"F0.wireOp",EDGE,"E8.8.0"),sQuery(id+"F0.wireOp",EDGE,"E8.8.2"),sQuery(id+"F0.wireOp",EDGE,"E8.9.0"),sQuery(id+"F0.wireOp",EDGE,"E8.9.2")])]});
            transform(context, id + "F10", {"entities" : qUnion([Q0]), "transformType" : TransformType.TRANSLATION_3D, "dx" : 0 * mm, "dy" : -26.3 * mm, "dz" : 0 * mm, "makeCopy" : true});
        }
    });
